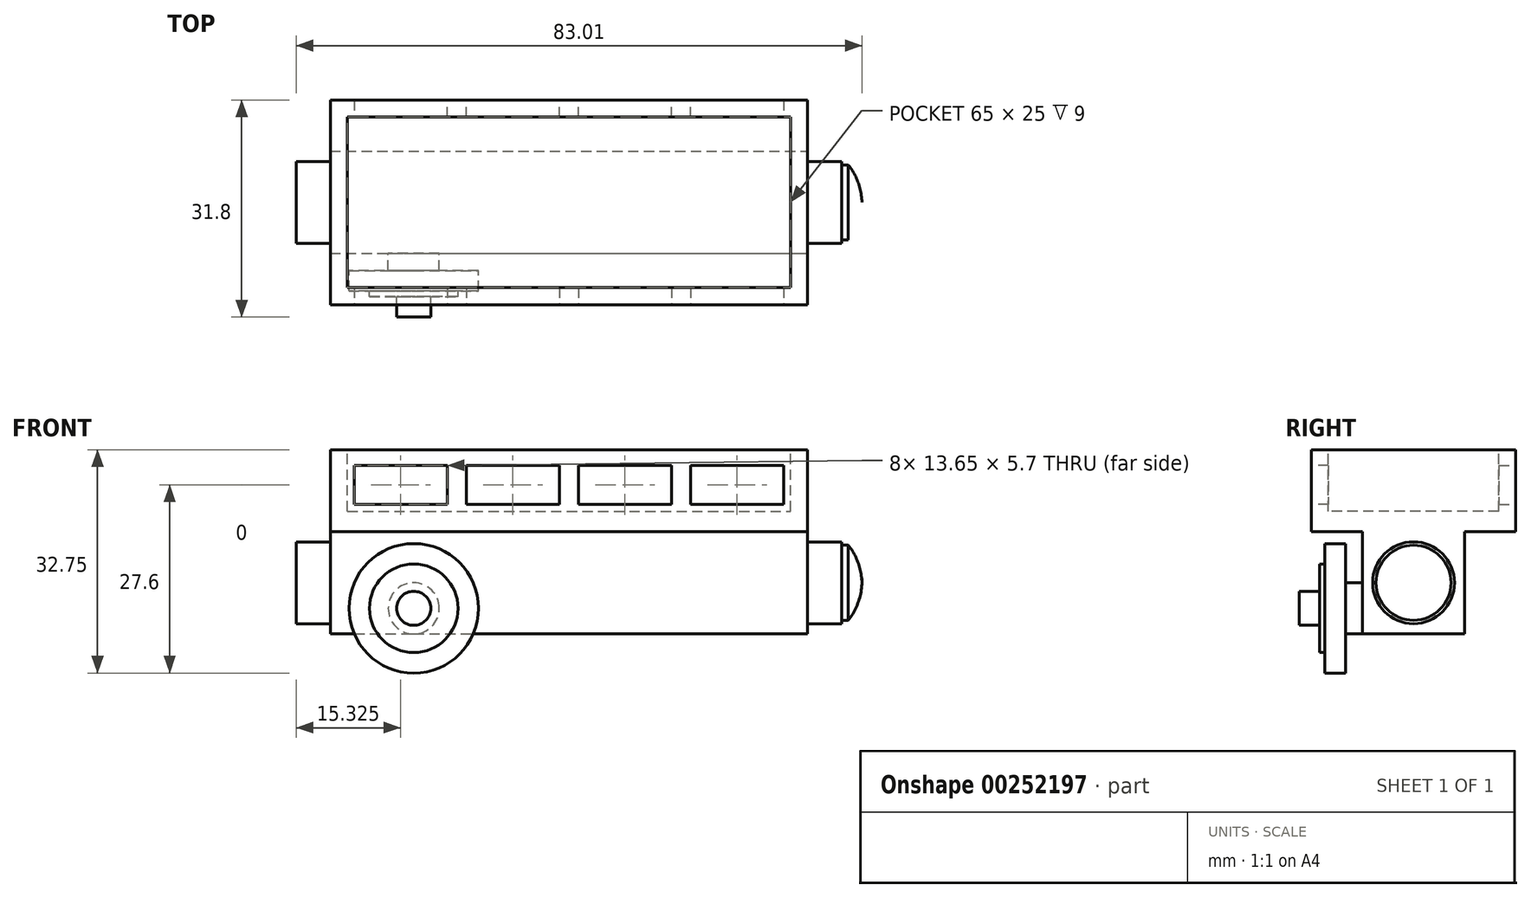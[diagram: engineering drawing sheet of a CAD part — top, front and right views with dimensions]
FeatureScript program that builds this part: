
annotation { "Feature Type Name" : "Feature", "Feature Type Description" : "" }
export const myFeature = defineFeature(function(context is Context, id is Id, definition is map)
    precondition{}
    {
        {
            var Q0;
            Q0=qCreatedBy(makeId("Top.planeOp"),FACE);
            var sketch = newSketch(context, id + "F0", { "sketchPlane" : qUnion([Q0])});
            skLineSegment(sketch, "E0.bottom", {"start": v(35, 15) * mm, "end": v(-35, 15) * mm});
            skLineSegment(sketch, "E0.top", {"start": v(35, -15) * mm, "end": v(-35, -15) * mm});
            skLineSegment(sketch, "E0.left", {"start": v(35, 15) * mm, "end": v(35, -15) * mm});
            skLineSegment(sketch, "E0.right", {"start": v(-35, 15) * mm, "end": v(-35, -15) * mm});
            skPoint(sketch, "E0.middle", {"position": v(0, 0) * mm});
            skSolve(sketch);
        }
        {
            var Q0;
            Q0 = qSketchRegion(id + "F0", true);
            extrude(context, id + "F1", {"entities" : qUnion([Q0]), "depth" : 12 * mm});
        }
        {
            var Q0;
            Q0=makeQuery(id+"F1.opExtrude","CAP_FACE",FACE,{"disambiguationData":[OSD([sQuery(id+"F0.wireOp",EDGE,"E0.bottom"),sQuery(id+"F0.wireOp",EDGE,"E0.top"),sQuery(id+"F0.wireOp",EDGE,"E0.left"),sQuery(id+"F0.wireOp",EDGE,"E0.right")])],"isStart":false});
            var sketch = newSketch(context, id + "F2", { "sketchPlane" : qUnion([Q0])});
            skLineSegment(sketch, "E1.bottom", {"start": v(-32.5, 12.5) * mm, "end": v(32.5, 12.5) * mm});
            skLineSegment(sketch, "E1.top", {"start": v(-32.5, -12.5) * mm, "end": v(32.5, -12.5) * mm});
            skLineSegment(sketch, "E1.left", {"start": v(-32.5, 12.5) * mm, "end": v(-32.5, -12.5) * mm});
            skLineSegment(sketch, "E1.right", {"start": v(32.5, 12.5) * mm, "end": v(32.5, -12.5) * mm});
            skPoint(sketch, "E1.middle", {"position": v(0, 0) * mm});
            skSolve(sketch);
        }
        {
            var Q0;
            Q0 = qSketchRegion(id + "F2", true);
            extrude(context, id + "F3", {"entities" : qUnion([Q0]), "operationType" : NewBodyOperationType.REMOVE, "oppositeDirection" : true, "depth" : 8 * mm});
        }
        {
            var Q0;
            Q0=makeQuery(id+"F1.opExtrude","SWEPT_FACE",FACE,{"disambiguationData":[OSD([sQuery(id+"F0.wireOp",EDGE,"E0.top")])]});
            var sketch = newSketch(context, id + "F4", { "sketchPlane" : qUnion([Q0])});
            skLineSegment(sketch, "E2.bottom", {"start": v(-31.5, 9.7) * mm, "end": v(31.5, 9.7) * mm});
            skLineSegment(sketch, "E2.top", {"start": v(-31.5, 4) * mm, "end": v(31.5, 4) * mm});
            skLineSegment(sketch, "E2.left", {"start": v(-31.5, 9.7) * mm, "end": v(-31.5, 4) * mm});
            skLineSegment(sketch, "E2.right", {"start": v(31.5, 9.7) * mm, "end": v(31.5, 4) * mm});
            skSolve(sketch);
        }
        {
            var Q0;
            Q0 = qSketchRegion(id + "F4", true);
            extrude(context, id + "F5", {"entities" : qUnion([Q0]), "operationType" : NewBodyOperationType.REMOVE, "oppositeDirection" : true, "depth" : 50 * mm});
        }
        {
            var Q0;
            Q0=makeQuery(id+"F5.boolean.opBoolean","MERGE",FACE,{"derivedFrom":[makeQuery(id+"F3.boolean.opBoolean","COPY",FACE,{"derivedFrom":makeQuery(id+"F3.opExtrude","CAP_FACE",FACE,{"disambiguationData":[OSD([sQuery(id+"F2.wireOp",EDGE,"E1.bottom"),sQuery(id+"F2.wireOp",EDGE,"E1.top"),sQuery(id+"F2.wireOp",EDGE,"E1.left"),sQuery(id+"F2.wireOp",EDGE,"E1.right")])],"isStart":false})}),makeQuery(id+"F5.opExtrude","SWEPT_FACE",FACE,{"disambiguationData":[OSD([sQuery(id+"F4.wireOp",EDGE,"E2.top")])]})]});
            var sketch = newSketch(context, id + "F6", { "sketchPlane" : qUnion([Q0])});
            skLineSegment(sketch, "E3.bottom", {"start": v(-32.5, 12.5) * mm, "end": v(32.5, 12.5) * mm});
            skLineSegment(sketch, "E3.top", {"start": v(-32.5, -12.5) * mm, "end": v(32.5, -12.5) * mm});
            skLineSegment(sketch, "E3.left", {"start": v(-32.5, 12.5) * mm, "end": v(-32.5, -12.5) * mm});
            skLineSegment(sketch, "E3.right", {"start": v(32.5, 12.5) * mm, "end": v(32.5, -12.5) * mm});
            skSolve(sketch);
        }
        {
            var Q0;
            Q0 = qSketchRegion(id + "F6", true);
            extrude(context, id + "F7", {"entities" : qUnion([Q0]), "operationType" : NewBodyOperationType.REMOVE, "oppositeDirection" : true, "depth" : 1 * mm});
        }
        {
            var Q0;
            Q0=makeQuery(id+"F1.opExtrude","SWEPT_FACE",FACE,{"disambiguationData":[OSD([sQuery(id+"F0.wireOp",EDGE,"E0.top")])]});
            var sketch = newSketch(context, id + "F8", { "sketchPlane" : qUnion([Q0])});
            skLineSegment(sketch, "E4.bottom", {"start": v(-1.4, 9.7) * mm, "end": v(1.4, 9.7) * mm});
            skLineSegment(sketch, "E4.top", {"start": v(-1.4, 4) * mm, "end": v(1.4, 4) * mm});
            skLineSegment(sketch, "E4.left", {"start": v(-1.4, 9.7) * mm, "end": v(-1.4, 4) * mm});
            skLineSegment(sketch, "E4.right", {"start": v(1.4, 9.7) * mm, "end": v(1.4, 4) * mm});
            skSolve(sketch);
        }
        {
            var Q0;
            Q0 = qSketchRegion(id + "F8", true);
            var Q1;
            {var subQ1=sQuery(id+"F2.wireOp",EDGE,"E1.top");var subQ3=makeQuery(id+"F1.opExtrude","SWEPT_FACE",FACE,{"disambiguationData":[OSD([sQuery(id+"F0.wireOp",EDGE,"E0.top")])]});var subQ4=makeQuery(id+"F3.boolean.opBoolean","COPY",FACE,{"derivedFrom":makeQuery(id+"F3.opExtrude","CAP_FACE",FACE,{"disambiguationData":[OSD([sQuery(id+"F2.wireOp",EDGE,"E1.bottom"),subQ1,sQuery(id+"F2.wireOp",EDGE,"E1.left"),sQuery(id+"F2.wireOp",EDGE,"E1.right")])],"isStart":false})});var subQ5=makeQuery(id+"F5.opExtrude","SWEPT_FACE",FACE,{"disambiguationData":[OSD([sQuery(id+"F4.wireOp",EDGE,"E2.top")])]});Q1=makeQuery(id+"F7.boolean.opBoolean","SPLIT",FACE,{"disambiguationData":[TD([subQ3])],"derivedFrom":makeQuery(id+"F5.boolean.opBoolean","MERGE",FACE,{"derivedFrom":[subQ4,subQ5]})});}
            extrude(context, id + "F9", {"entities" : qUnion([Q0]), "operationType" : NewBodyOperationType.ADD, "oppositeDirection" : true, "endBoundEntityFace" : qUnion([Q1]), "depth" : 2.5 * mm});
        }
        {
            var Q0;
            Q0=makeQuery(id+"F9.boolean.opBoolean","MERGE",FACE,{"derivedFrom":[makeQuery(id+"F1.opExtrude","SWEPT_FACE",FACE,{"disambiguationData":[OSD([sQuery(id+"F0.wireOp",EDGE,"E0.top")])]}),makeQuery(id+"F9.opExtrude","CAP_FACE",FACE,{"disambiguationData":[OSD([sQuery(id+"F8.wireOp",EDGE,"E4.bottom"),sQuery(id+"F8.wireOp",EDGE,"E4.top"),sQuery(id+"F8.wireOp",EDGE,"E4.left"),sQuery(id+"F8.wireOp",EDGE,"E4.right")])],"isStart":true})]});
            var sketch = newSketch(context, id + "F10", { "sketchPlane" : qUnion([Q0])});
            skLineSegment(sketch, "E5", {"start": v(16.45, 4) * mm, "end": v(16.45, 9.7) * mm, "construction": true});
            skLineSegment(sketch, "E6.bottom", {"start": v(15.05, 9.7) * mm, "end": v(17.85, 9.7) * mm});
            skLineSegment(sketch, "E6.top", {"start": v(15.05, 4) * mm, "end": v(17.85, 4) * mm});
            skLineSegment(sketch, "E6.left", {"start": v(15.05, 9.7) * mm, "end": v(15.05, 4) * mm});
            skLineSegment(sketch, "E6.right", {"start": v(17.85, 9.7) * mm, "end": v(17.85, 4) * mm});
            skSolve(sketch);
        }
        {
            var Q0;
            Q0 = qSketchRegion(id + "F10", true);
            extrude(context, id + "F11", {"entities" : qUnion([Q0]), "operationType" : NewBodyOperationType.ADD, "oppositeDirection" : true, "depth" : 2.5 * mm});
        }
        {
            var Q0;
            Q0=makeQuery(id+"F11.boolean.opBoolean","MERGE",FACE,{"derivedFrom":[makeQuery(id+"F9.boolean.opBoolean","MERGE",FACE,{"derivedFrom":[makeQuery(id+"F1.opExtrude","SWEPT_FACE",FACE,{"disambiguationData":[OSD([sQuery(id+"F0.wireOp",EDGE,"E0.top")])]}),makeQuery(id+"F9.opExtrude","CAP_FACE",FACE,{"disambiguationData":[OSD([sQuery(id+"F8.wireOp",EDGE,"E4.bottom"),sQuery(id+"F8.wireOp",EDGE,"E4.top"),sQuery(id+"F8.wireOp",EDGE,"E4.left"),sQuery(id+"F8.wireOp",EDGE,"E4.right")])],"isStart":true})]}),makeQuery(id+"F11.opExtrude","CAP_FACE",FACE,{"disambiguationData":[OSD([sQuery(id+"F10.wireOp",EDGE,"E6.bottom"),sQuery(id+"F10.wireOp",EDGE,"E6.top"),sQuery(id+"F10.wireOp",EDGE,"E6.left"),sQuery(id+"F10.wireOp",EDGE,"E6.right")])],"isStart":true})]});
            var sketch = newSketch(context, id + "F12", { "sketchPlane" : qUnion([Q0])});
            skLineSegment(sketch, "E7", {"start": v(-16.45, 9.7) * mm, "end": v(-16.45, 4) * mm, "construction": true});
            skLineSegment(sketch, "E8.bottom", {"start": v(-15.05, 9.7) * mm, "end": v(-17.85, 9.7) * mm});
            skLineSegment(sketch, "E8.top", {"start": v(-15.05, 4) * mm, "end": v(-17.85, 4) * mm});
            skLineSegment(sketch, "E8.left", {"start": v(-15.05, 9.7) * mm, "end": v(-15.05, 4) * mm});
            skLineSegment(sketch, "E8.right", {"start": v(-17.85, 9.7) * mm, "end": v(-17.85, 4) * mm});
            skSolve(sketch);
        }
        {
            var Q0;
            Q0 = qSketchRegion(id + "F12", true);
            extrude(context, id + "F13", {"entities" : qUnion([Q0]), "operationType" : NewBodyOperationType.ADD, "oppositeDirection" : true, "depth" : 2.5 * mm});
        }
        {
            var Q0;
            Q0=makeQuery(id+"F1.opExtrude","SWEPT_FACE",FACE,{"disambiguationData":[OSD([sQuery(id+"F0.wireOp",EDGE,"E0.bottom")])]});
            var sketch = newSketch(context, id + "F14", { "sketchPlane" : qUnion([Q0])});
            skLineSegment(sketch, "E9.bottom", {"start": v(-1.4, 9.7) * mm, "end": v(1.4, 9.7) * mm});
            skLineSegment(sketch, "E9.top", {"start": v(-1.4, 4) * mm, "end": v(1.4, 4) * mm});
            skLineSegment(sketch, "E9.left", {"start": v(-1.4, 9.7) * mm, "end": v(-1.4, 4) * mm});
            skLineSegment(sketch, "E9.right", {"start": v(1.4, 9.7) * mm, "end": v(1.4, 4) * mm});
            skSolve(sketch);
        }
        {
            var Q0;
            Q0 = qSketchRegion(id + "F14", true);
            extrude(context, id + "F15", {"entities" : qUnion([Q0]), "operationType" : NewBodyOperationType.ADD, "oppositeDirection" : true, "depth" : 2.5 * mm});
        }
        {
            var Q0;
            Q0=makeQuery(id+"F15.boolean.opBoolean","MERGE",FACE,{"derivedFrom":[makeQuery(id+"F1.opExtrude","SWEPT_FACE",FACE,{"disambiguationData":[OSD([sQuery(id+"F0.wireOp",EDGE,"E0.bottom")])]}),makeQuery(id+"F15.opExtrude","CAP_FACE",FACE,{"disambiguationData":[OSD([sQuery(id+"F14.wireOp",EDGE,"E9.bottom"),sQuery(id+"F14.wireOp",EDGE,"E9.top"),sQuery(id+"F14.wireOp",EDGE,"E9.left"),sQuery(id+"F14.wireOp",EDGE,"E9.right")])],"isStart":true})]});
            var sketch = newSketch(context, id + "F16", { "sketchPlane" : qUnion([Q0])});
            skLineSegment(sketch, "E10", {"start": v(-16.45, 9.7) * mm, "end": v(-16.45, 4) * mm, "construction": true});
            skLineSegment(sketch, "E11.bottom", {"start": v(-17.85, 9.7) * mm, "end": v(-15.05, 9.7) * mm});
            skLineSegment(sketch, "E11.top", {"start": v(-17.85, 4) * mm, "end": v(-15.05, 4) * mm});
            skLineSegment(sketch, "E11.left", {"start": v(-17.85, 9.7) * mm, "end": v(-17.85, 4) * mm});
            skLineSegment(sketch, "E11.right", {"start": v(-15.05, 9.7) * mm, "end": v(-15.05, 4) * mm});
            skSolve(sketch);
        }
        {
            var Q0;
            Q0 = qSketchRegion(id + "F16", true);
            extrude(context, id + "F17", {"entities" : qUnion([Q0]), "operationType" : NewBodyOperationType.ADD, "oppositeDirection" : true, "depth" : 2.5 * mm});
        }
        {
            var Q0;
            Q0=makeQuery(id+"F17.boolean.opBoolean","MERGE",FACE,{"derivedFrom":[makeQuery(id+"F15.boolean.opBoolean","MERGE",FACE,{"derivedFrom":[makeQuery(id+"F1.opExtrude","SWEPT_FACE",FACE,{"disambiguationData":[OSD([sQuery(id+"F0.wireOp",EDGE,"E0.bottom")])]}),makeQuery(id+"F15.opExtrude","CAP_FACE",FACE,{"disambiguationData":[OSD([sQuery(id+"F14.wireOp",EDGE,"E9.bottom"),sQuery(id+"F14.wireOp",EDGE,"E9.top"),sQuery(id+"F14.wireOp",EDGE,"E9.left"),sQuery(id+"F14.wireOp",EDGE,"E9.right")])],"isStart":true})]}),makeQuery(id+"F17.opExtrude","CAP_FACE",FACE,{"disambiguationData":[OSD([sQuery(id+"F16.wireOp",EDGE,"E11.bottom"),sQuery(id+"F16.wireOp",EDGE,"E11.top"),sQuery(id+"F16.wireOp",EDGE,"E11.left"),sQuery(id+"F16.wireOp",EDGE,"E11.right")])],"isStart":true})]});
            var sketch = newSketch(context, id + "F18", { "sketchPlane" : qUnion([Q0])});
            skLineSegment(sketch, "E12", {"start": v(16.45, 9.7) * mm, "end": v(16.45, 4) * mm, "construction": true});
            skLineSegment(sketch, "E13.bottom", {"start": v(15.05, 9.7) * mm, "end": v(17.85, 9.7) * mm});
            skLineSegment(sketch, "E13.top", {"start": v(15.05, 4) * mm, "end": v(17.85, 4) * mm});
            skLineSegment(sketch, "E13.left", {"start": v(15.05, 9.7) * mm, "end": v(15.05, 4) * mm});
            skLineSegment(sketch, "E13.right", {"start": v(17.85, 9.7) * mm, "end": v(17.85, 4) * mm});
            skSolve(sketch);
        }
        {
            var Q0;
            Q0 = qSketchRegion(id + "F18", true);
            extrude(context, id + "F19", {"entities" : qUnion([Q0]), "operationType" : NewBodyOperationType.ADD, "oppositeDirection" : true, "depth" : 2.5 * mm});
        }
        {
            var Q0;
            Q0=makeQuery(id+"F1.opExtrude","CAP_FACE",FACE,{"disambiguationData":[OSD([sQuery(id+"F0.wireOp",EDGE,"E0.bottom"),sQuery(id+"F0.wireOp",EDGE,"E0.top"),sQuery(id+"F0.wireOp",EDGE,"E0.left"),sQuery(id+"F0.wireOp",EDGE,"E0.right")])],"isStart":true});
            var sketch = newSketch(context, id + "F20", { "sketchPlane" : qUnion([Q0])});
            skLineSegment(sketch, "E14.bottom", {"start": v(-35, 7.5) * mm, "end": v(35, 7.5) * mm});
            skLineSegment(sketch, "E14.top", {"start": v(-35, -7.5) * mm, "end": v(35, -7.5) * mm});
            skLineSegment(sketch, "E14.left", {"start": v(-35, 7.5) * mm, "end": v(-35, -7.5) * mm});
            skLineSegment(sketch, "E14.right", {"start": v(35, 7.5) * mm, "end": v(35, -7.5) * mm});
            skSolve(sketch);
        }
        {
            var Q0;
            Q0 = qSketchRegion(id + "F20", true);
            extrude(context, id + "F21", {"entities" : qUnion([Q0]), "operationType" : NewBodyOperationType.ADD, "depth" : 15 * mm});
        }
        {
            var Q0;
            Q0=makeQuery(id+"F21.opExtrude","SWEPT_FACE",FACE,{"disambiguationData":[OSD([sQuery(id+"F20.wireOp",EDGE,"E14.right")])]});
            var sketch = newSketch(context, id + "F22", { "sketchPlane" : qUnion([Q0])});
            skLineSegment(sketch, "E15", {"start": v(0, 0) * mm, "end": v(0, -15) * mm, "construction": true});
            skLineSegment(sketch, "E16", {"start": v(-7.5, -7.5) * mm, "end": v(7.5, -7.5) * mm, "construction": true});
            skCircle(sketch, "E17", {"center": v(0, -7.5) * mm, "radius": 6 * mm});
            skSolve(sketch);
        }
        {
            var Q0;
            Q0 = qSketchRegion(id + "F22", true);
            extrude(context, id + "F23", {"entities" : qUnion([Q0]), "operationType" : NewBodyOperationType.ADD, "depth" : 5 * mm});
        }
        {
            var Q0;
            Q0=makeQuery(id+"F21.boolean.opBoolean","MERGE",FACE,{"derivedFrom":[makeQuery(id+"F1.opExtrude","SWEPT_FACE",FACE,{"disambiguationData":[OSD([sQuery(id+"F0.wireOp",EDGE,"E0.right")])]}),makeQuery(id+"F21.opExtrude","SWEPT_FACE",FACE,{"disambiguationData":[OSD([sQuery(id+"F20.wireOp",EDGE,"E14.left")])]})]});
            var sketch = newSketch(context, id + "F24", { "sketchPlane" : qUnion([Q0])});
            skLineSegment(sketch, "E18", {"start": v(0, 0) * mm, "end": v(0, -15) * mm, "construction": true});
            skLineSegment(sketch, "E19", {"start": v(-7.5, -7.5) * mm, "end": v(7.5, -7.5) * mm, "construction": true});
            skCircle(sketch, "E20", {"center": v(0, -7.5) * mm, "radius": 6 * mm});
            skSolve(sketch);
        }
        {
            var Q0;
            Q0 = qSketchRegion(id + "F24", true);
            extrude(context, id + "F25", {"entities" : qUnion([Q0]), "operationType" : NewBodyOperationType.ADD, "depth" : 5 * mm});
        }
        {
            var Q0;
            Q0=makeQuery(id+"F23.opExtrude","CAP_FACE",FACE,{"disambiguationData":[OSD([sQuery(id+"F22.wireOp",EDGE,"E17")])],"isStart":false});
            var sketch = newSketch(context, id + "F26", { "sketchPlane" : qUnion([Q0])});
            skCircle(sketch, "E21", {"center": v(0, -7.5) * mm, "radius": 5.5 * mm});
            skSolve(sketch);
        }
        {
            var Q0;
            Q0 = qSketchRegion(id + "F26", true);
            extrude(context, id + "F27", {"entities" : qUnion([Q0]), "operationType" : NewBodyOperationType.ADD, "depth" : 1 * mm});
        }
        {
            var Q0;
            Q0=makeQuery(id+"F27.opExtrude","CAP_FACE",FACE,{"disambiguationData":[OSD([sQuery(id+"F26.wireOp",EDGE,"E21")])],"isStart":false});
            var sketch = newSketch(context, id + "F28", { "sketchPlane" : qUnion([Q0])});
            skLineSegment(sketch, "E22", {"start": v(0, -13) * mm, "end": v(0, -2) * mm, "construction": true});
            skSolve(sketch);
        }
        {
            var Q0;
            Q0=qCreatedBy(makeId("Front.planeOp"),FACE);
            var sketch = newSketch(context, id + "F29", { "sketchPlane" : qUnion([Q0])});
            skPoint(sketch, "E23.0", {"position": v(41, -7.5) * mm});
            skLineSegment(sketch, "E24", {"start": v(41, -7.5) * mm, "end": v(43, -7.5) * mm});
            skPoint(sketch, "E25.0", {"position": v(41, -13) * mm});
            skArc(sketch, "E26", {"start": v(41, -13) * mm, "mid": v(42.44, -10.4) * mm, "end": v(43, -7.5) * mm});
            skLineSegment(sketch, "E27", {"start": v(41, -7.5) * mm, "end": v(41, -13) * mm});
            skSolve(sketch);
        }
        {
            var Q0;
            Q0 = qSketchRegion(id + "F29", true);
            var Q1;
            Q1=sQuery(id+"F29.wireOp",EDGE,"E24");
            revolve(context, id + "F30", {"operationType" : NewBodyOperationType.ADD, "entities" : qUnion([Q0]), "axis" : qUnion([Q1]), "revolveType" : RevolveType.FULL});
        }
        {
            var Q0;
            Q0=makeQuery(id+"F21.opExtrude","SWEPT_FACE",FACE,{"disambiguationData":[OSD([sQuery(id+"F20.wireOp",EDGE,"E14.bottom")])]});
            var sketch = newSketch(context, id + "F31", { "sketchPlane" : qUnion([Q0])});
            skCircle(sketch, "E28", {"center": v(-22.75, -11.25) * mm, "radius": 3.75 * mm});
            skSolve(sketch);
        }
        {
            var Q0;
            Q0 = qSketchRegion(id + "F31", true);
            extrude(context, id + "F32", {"entities" : qUnion([Q0]), "operationType" : NewBodyOperationType.ADD, "depth" : 2.5 * mm});
        }
        {
            var Q0;
            Q0=makeQuery(id+"F32.opExtrude","CAP_FACE",FACE,{"disambiguationData":[OSD([sQuery(id+"F31.wireOp",EDGE,"E28")])],"isStart":false});
            var sketch = newSketch(context, id + "F33", { "sketchPlane" : qUnion([Q0])});
            skCircle(sketch, "E29", {"center": v(-22.75, -11.25) * mm, "radius": 9.5 * mm});
            skSolve(sketch);
        }
        {
            var Q0;
            Q0 = qSketchRegion(id + "F33", true);
            extrude(context, id + "F34", {"entities" : qUnion([Q0]), "operationType" : NewBodyOperationType.ADD, "depth" : 3 * mm});
        }
        {
            var Q0;
            Q0=makeQuery(id+"F34.opExtrude","CAP_FACE",FACE,{"disambiguationData":[OSD([sQuery(id+"F33.wireOp",EDGE,"E29")])],"isStart":false});
            var sketch = newSketch(context, id + "F35", { "sketchPlane" : qUnion([Q0])});
            skCircle(sketch, "E30", {"center": v(-22.75, -11.25) * mm, "radius": 6.5 * mm});
            skSolve(sketch);
        }
        {
            var Q0;
            Q0 = qSketchRegion(id + "F35", true);
            extrude(context, id + "F36", {"entities" : qUnion([Q0]), "operationType" : NewBodyOperationType.ADD, "depth" : 0.8 * mm});
        }
        {
            var Q0;
            Q0=makeQuery(id+"F36.opExtrude","CAP_FACE",FACE,{"disambiguationData":[OSD([sQuery(id+"F35.wireOp",EDGE,"E30")])],"isStart":false});
            var sketch = newSketch(context, id + "F37", { "sketchPlane" : qUnion([Q0])});
            skCircle(sketch, "E31", {"center": v(-22.75, -11.25) * mm, "radius": 2.5 * mm});
            skSolve(sketch);
        }
        {
            var Q0;
            Q0 = qSketchRegion(id + "F37", true);
            extrude(context, id + "F38", {"entities" : qUnion([Q0]), "operationType" : NewBodyOperationType.ADD, "depth" : 3 * mm});
        }
    });
